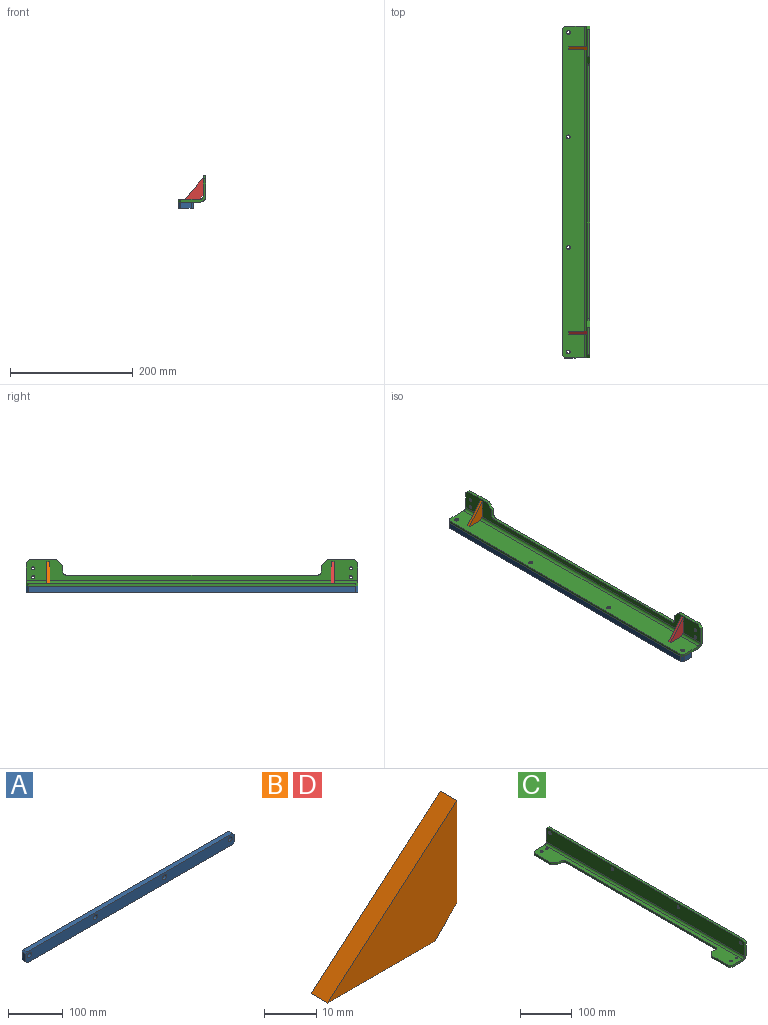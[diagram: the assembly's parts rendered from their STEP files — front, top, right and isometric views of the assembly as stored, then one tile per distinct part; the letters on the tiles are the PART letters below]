
ASSEMBLY  parts=4 mates=6
PART A: 22 faces, bbox 540x10x25 mm
  f0: plane 532x10mm, normal (0,0,-1), area 5320mm2, adj f4,f5,f6,f8
  f1: plane 17x10mm, normal (1,0,0), area 170mm2, adj f4,f5,f6,f7
  f2: plane 532x10mm, normal (0,0,1), area 5320mm2, adj f4,f5,f7,f9
  f3: plane 17x10mm, normal (-1,0,0), area 170mm2, adj f4,f5,f8,f9
  f4: plane 540x25mm, normal (0,-1,0), area 13087.9mm2, adj f0,f1,f2,f3,f6,f7,f8,f9
  f5: plane 540x25mm, normal (0,1,0), area 13331.2mm2, adj f0,f1,f2,f3,f6,f7,f8,f9
  f6: plane 10x4mm, normal (0.71,0,-0.71), area 56.6mm2, adj f0,f1,f4,f5
  f7: plane 10x4mm, normal (0.71,0,0.71), area 56.6mm2, adj f1,f2,f4,f5
  f8: plane 10x4mm, normal (-0.71,0,-0.71), area 56.6mm2, adj f0,f3,f4,f5
  f9: plane 10x4mm, normal (-0.71,0,0.71), area 56.6mm2, adj f2,f3,f4,f5
  f10: cylinder r=3.3mm len=6.6mm, axis (0,-1,0), area 72.6mm2, adj f5,f11
  f11: plane 11x11mm, normal (0,-1,0), area 60.8mm2, adj f10,f12
  f12: cylinder r=5.5mm len=11mm, axis (0,-1,0), area 224.6mm2, adj f4,f11
  f13: cylinder r=3.3mm len=6.6mm, axis (0,-1,0), area 72.6mm2, adj f5,f14
  f14: plane 11x11mm, normal (0,-1,0), area 60.8mm2, adj f13,f15
  f15: cylinder r=5.5mm len=11mm, axis (0,-1,0), area 224.6mm2, adj f4,f14
  f16: cylinder r=3.3mm len=6.6mm, axis (0,-1,0), area 72.6mm2, adj f5,f17
  f17: plane 11x11mm, normal (0,-1,0), area 60.8mm2, adj f16,f18
  f18: cylinder r=5.5mm len=11mm, axis (0,-1,0), area 224.6mm2, adj f4,f17
  f19: cylinder r=3.3mm len=6.6mm, axis (0,-1,0), area 72.6mm2, adj f5,f20
  f20: plane 11x11mm, normal (0,-1,0), area 60.8mm2, adj f19,f21
  f21: cylinder r=5.5mm len=11mm, axis (0,-1,0), area 224.6mm2, adj f4,f20
PART B: 6 faces, bbox 35x4.5x30 mm
  f0: plane 29x4.5mm, normal (0,0,-1), area 130.5mm2, adj f2,f3,f4,f5
  f1: plane 24x4.5mm, normal (1,0,0), area 108mm2, adj f2,f3,f4,f5
  f2: plane 35x30mm, normal (-0.65,0,0.76), area 207.4mm2, adj f0,f1,f3,f4
  f3: plane 35x30mm, normal (0,-1,0), area 507mm2, adj f0,f1,f2,f5
  f4: plane 35x30mm, normal (0,1,0), area 507mm2, adj f0,f1,f2,f5
  f5: plane 6x6mm, normal (0.71,0,-0.71), area 38.2mm2, adj f0,f1,f3,f4
PART C: 54 faces, bbox 43.7x540.3x45.7 mm
  f0: plane 540.29x36.29mm, normal (-1,0,0), area 19307.4mm2, adj f5,f6,f9,f10,f34,f35,f36,f37
  f1: plane 540.29x36.29mm, normal (1,0,0), area 19307.4mm2, adj f5,f8,f9,f10,f34,f35,f36,f37
  f2: plane 45x4.5mm, normal (-1,0,0), area 202.5mm2, adj f3,f4,f28,f52
  f3: plane 540.29x34.29mm, normal (0,0,1), area 7667.3mm2, adj f2,f5,f6,f7,f10,f11,f12,f13
  f4: plane 540.29x34.29mm, normal (0,0,-1), area 7667.3mm2, adj f2,f5,f7,f8,f10,f11,f12,f13
  f5: plane 41x38mm, normal (0,1,0), area 322.2mm2, adj f0,f1,f3,f4,f6,f8,f28,f51
  f6: cylinder r=4.5mm len=540mm, axis (0,1,0), area 3817mm2, adj f0,f3,f5,f10
  f7: plane 45x4.5mm, normal (-1,0,0), area 202.5mm2, adj f3,f4,f11,f53
  f8: cylinder r=9mm len=540mm, axis (0,1,0), area 7634.1mm2, adj f1,f4,f5,f10
  f9: plane 532x4.5mm, normal (0,0,1), area 2394mm2, adj f0,f1,f50,f51
  f10: plane 41x38mm, normal (0,-1,0), area 322.2mm2, adj f0,f1,f3,f4,f6,f8,f11,f50
  f11: plane 5x5mm, normal (-0.71,-0.71,0), area 31.8mm2, adj f3,f4,f7,f10
  f12: bspline ~6.45x5.58mm, area 44.7mm2, adj f3,f4,f14,f15
  f13: bspline ~6.45x5.58mm, area 44.6mm2, adj f3,f4,f14,f15
  f14: bspline ~6.55x5.67mm, area 11.5mm2, adj f3,f4,f12,f13
  f15: cylinder r=2.25mm len=4.5mm, axis (0,0,-1), area 16.1mm2, adj f3,f4,f12,f13
  f16: bspline ~6.45x5.58mm, area 44.7mm2, adj f3,f4,f18,f19
  f17: bspline ~6.45x5.58mm, area 44.6mm2, adj f3,f4,f18,f19
  f18: bspline ~6.55x5.67mm, area 11.5mm2, adj f3,f4,f16,f17
  f19: cylinder r=2.25mm len=4.5mm, axis (0,0,-1), area 16.1mm2, adj f3,f4,f16,f17
  f20: cylinder r=2.25mm len=4.5mm, axis (0,0,-1), area 15.7mm2, adj f3,f4,f21,f23
  f21: bspline ~6.45x5.58mm, area 44.6mm2, adj f3,f4,f20,f22
  f22: bspline ~6.55x5.67mm, area 11.5mm2, adj f3,f4,f21,f23
  f23: bspline ~6.45x5.58mm, area 44.7mm2, adj f3,f4,f20,f22
  f24: cylinder r=2.25mm len=4.5mm, axis (0,0,-1), area 15.7mm2, adj f3,f4,f25,f27
  f25: bspline ~6.45x5.58mm, area 44.6mm2, adj f3,f4,f24,f26
  f26: bspline ~6.55x5.67mm, area 11.5mm2, adj f3,f4,f25,f27
  f27: bspline ~6.45x5.58mm, area 44.7mm2, adj f3,f4,f24,f26
  f28: plane 5x5mm, normal (-0.71,0.71,0), area 31.8mm2, adj f2,f3,f4,f5
  f29: plane 10x4.5mm, normal (0,1,0), area 45mm2, adj f3,f4,f30,f53
  f30: cylinder r=5mm len=5mm, axis (0,0,1), area 35.3mm2, adj f3,f4,f29,f31
  f31: plane 410x4.5mm, normal (-1,0,0), area 1845mm2, adj f3,f4,f30,f32
  f32: cylinder r=5mm len=5mm, axis (0,0,1), area 35.3mm2, adj f3,f4,f31,f33
  f33: plane 10x4.5mm, normal (0,-1,0), area 45mm2, adj f3,f4,f32,f52
  f34: bspline ~7.72x6.68mm, area 54.4mm2, adj f0,f1,f36,f37
  f35: bspline ~7.72x6.68mm, area 54.3mm2, adj f0,f1,f36,f37
  f36: bspline ~7.82x6.77mm, area 13.8mm2, adj f0,f1,f34,f35
  f37: cylinder r=2.8mm len=5.6mm, axis (1,0,0), area 20.1mm2, adj f0,f1,f34,f35
  f38: bspline ~7.72x6.68mm, area 54.4mm2, adj f0,f1,f40,f41
  f39: bspline ~7.72x6.68mm, area 54.3mm2, adj f0,f1,f40,f41
  f40: bspline ~7.82x6.77mm, area 13.8mm2, adj f0,f1,f38,f39
  f41: cylinder r=2.8mm len=5.6mm, axis (1,0,0), area 20.1mm2, adj f0,f1,f38,f39
  f42: bspline ~7.72x6.68mm, area 54.4mm2, adj f0,f1,f44,f45
  f43: bspline ~7.72x6.68mm, area 54.3mm2, adj f0,f1,f44,f45
  f44: bspline ~7.82x6.77mm, area 13.8mm2, adj f0,f1,f42,f43
  f45: cylinder r=2.8mm len=5.6mm, axis (1,0,0), area 20.1mm2, adj f0,f1,f42,f43
  f46: bspline ~7.72x6.68mm, area 54.4mm2, adj f0,f1,f48,f49
  f47: bspline ~7.72x6.68mm, area 54.3mm2, adj f0,f1,f48,f49
  f48: bspline ~7.82x6.77mm, area 13.8mm2, adj f0,f1,f46,f47
  f49: cylinder r=2.8mm len=5.6mm, axis (1,0,0), area 20.1mm2, adj f0,f1,f46,f47
  f50: plane 4.5x4mm, normal (0,-0.71,0.71), area 25.5mm2, adj f0,f1,f9,f10
  f51: plane 4.5x4mm, normal (0,0.71,0.71), area 25.5mm2, adj f0,f1,f5,f9
  f52: plane 10x10mm, normal (-0.71,-0.71,0), area 63.6mm2, adj f2,f3,f4,f33
  f53: plane 10x10mm, normal (-0.71,0.71,0), area 63.6mm2, adj f3,f4,f7,f29
PART D: same geometry as B
PLACE A rot(axis=(0.58,-0.58,-0.58),120deg) t=(-5.56,0,-5)mm
PLACE B rot(axis=(0.71,0,-0.71),180deg) t=(22.44,233.68,4.5)mm
PLACE C rot(axis=(-0.71,0,0.71),180deg) t=(26.94,0,0)mm
PLACE D rot(axis=(0.71,0,-0.71),180deg) t=(22.44,-228.99,4.5)mm
MATE parallel B.f0 <-> C.f3  axis (1,0,0) through (22.44,231.43,39.5)mm
MATE planar D.f0 <-> C.f3  axis (1,0,0) through (22.44,-228.99,25)mm
MATE planar B.f0 <-> C.f3  axis (1,0,0) through (22.44,233.68,25)mm
MATE planar C.f0 <-> B.f1  axis (0,0,1) through (0,0,4.5)mm
MATE planar A.f16 <-> C.f1  axis (0,0,1) through (-8.06,90,0)mm
MATE planar D.f1 <-> C.f0  axis (0,0,-1) through (4.44,-228.99,4.5)mm
